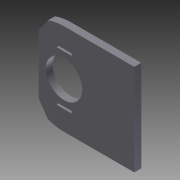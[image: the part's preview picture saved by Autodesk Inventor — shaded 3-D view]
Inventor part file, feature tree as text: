
AUTODESK INVENTOR PART (.ipt)
format: ipt  version: 2013 (Build 170138000, 138)  size: 90,624 bytes
history: native  units: in
note: dims shown in document units (in); Inventor stores cm internally (conversion verified against a paired STEP export)
features: reference x8, extrude x2, sketch x2
ambient origin geometry x8: Origin, YZ Plane, XZ Plane, XY Plane, X Axis, Y Axis, Z Axis, Center Point
bodies: Solid1 (feature_tree)
feature tree (12):
  extrude  "Extrusion1"  Depth=1.0in TaperAngle=0.0deg
  extrude  "Extrusion2"  [1 undecoded]
  sketch  "Sketch1"  dims[d0=0.039in d1=0.0in d2=1.0in d3=0.0in]
  sketch  "Sketch2"
  reference  "Reference1"
  reference  "Reference2"
  reference  "Reference3"
  reference  "Reference4"
  reference  "Reference5"
  reference  "Reference6"
  reference  "Reference7"
  reference  "Reference8"
note: 1 required parameter value undecoded (feature->parameter linkage not recoverable at this tier; creation-order binding heuristic only, values carry confidence <= 0.55)
